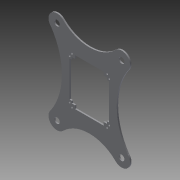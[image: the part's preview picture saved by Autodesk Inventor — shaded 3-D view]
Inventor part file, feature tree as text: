
AUTODESK INVENTOR PART (.ipt)
format: ipt  version: 2015 (Build 190159000, 159)  size: 138,240 bytes
history: native  units: mm
features: extrude x1, sketch x1
ambient origin geometry x8: Origin, YZ Plane, XZ Plane, XY Plane, X Axis, Y Axis, Z Axis, Center Point
bodies: Solid1 (feature_tree)
feature tree (2):
  extrude  "Extrusion1"  Depth=3.25mm
  sketch  "Sketch1"  dims[d0=3.25mm d1=3.25mm d2=4.625mm d3=4.625mm d4=2.0mm d5=0.0mm]
